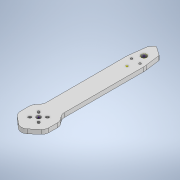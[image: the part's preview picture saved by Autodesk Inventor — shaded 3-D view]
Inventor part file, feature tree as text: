
AUTODESK INVENTOR PART (.ipt)
format: ipt  version: 2020 (Build 240168000, 168)  size: 171,008 bytes
history: native  units: mm
features: sketch x2, extrude x1
ambient origin geometry x8: Origin, YZ Plane, XZ Plane, XY Plane, X Axis, Y Axis, Z Axis, Center Point
bodies: Solid1 (feature_tree)
feature tree (3):
  extrude  "Extrusion1"  [1 undecoded]
  sketch  "Sketch2"
  sketch  "Sketch1"  dims[d0=6.0mm d1=0.0mm]
note: 1 required parameter value undecoded (feature->parameter linkage not recoverable at this tier; creation-order binding heuristic only, values carry confidence <= 0.55)
